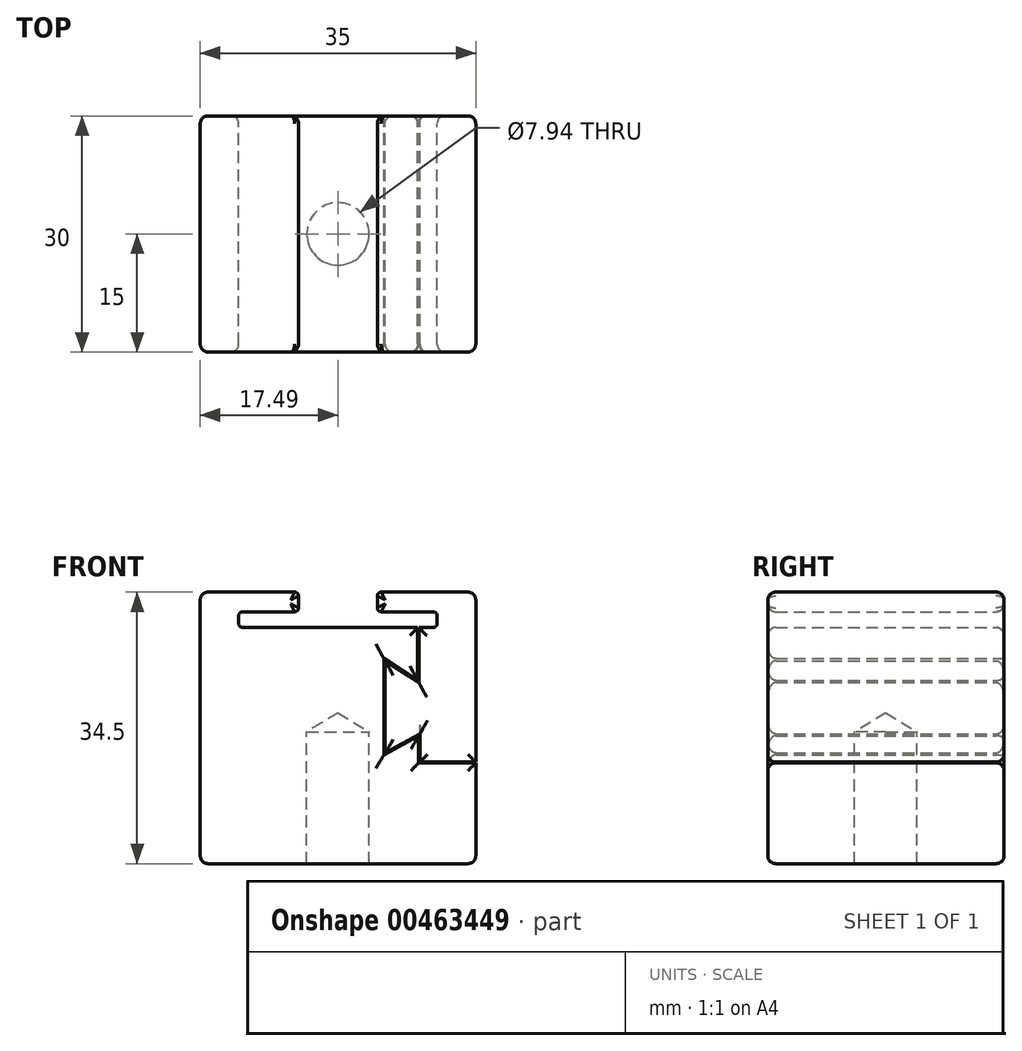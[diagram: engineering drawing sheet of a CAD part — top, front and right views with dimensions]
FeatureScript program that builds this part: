
annotation { "Feature Type Name" : "Feature", "Feature Type Description" : "" }
export const myFeature = defineFeature(function(context is Context, id is Id, definition is map)
    precondition{}
    {
        {
            var Q0;
            Q0=qCreatedBy(makeId("Front.planeOp"),FACE);
            var sketch = newSketch(context, id + "F0", { "sketchPlane" : qUnion([Q0])});
            skLineSegment(sketch, "E0.bottom", {"start": v(16.5, -15.75) * mm, "end": v(-16.5, -15.75) * mm});
            skLineSegment(sketch, "E0.top", {"start": v(16.5, 18.75) * mm, "end": v(5.5, 18.75) * mm});
            skLineSegment(sketch, "E0.left", {"start": v(17.5, -14.75) * mm, "end": v(17.5, -2.95) * mm});
            skLineSegment(sketch, "E0.right", {"start": v(-17.5, -14.75) * mm, "end": v(-17.5, 17.75) * mm});
            skPoint(sketch, "E1.middle", {"position": v(0, 0) * mm});
            skLineSegment(sketch, "E2.left", {"start": v(-5, 16.75) * mm, "end": v(-5, 18.25) * mm});
            skLineSegment(sketch, "E2.right", {"start": v(5, 16.75) * mm, "end": v(5, 18.25) * mm});
            skPoint(sketch, "E2.middle.positionSnap0", {"position": v(0, 18.75) * mm});
            skPoint(sketch, "E2.centerSnap0", {"position": v(0, 18.75) * mm});
            skLineSegment(sketch, "E3.bottom", {"start": v(12.1, 14.25) * mm, "end": v(10.29, 14.25) * mm});
            skLineSegment(sketch, "E3.top", {"start": v(12.1, 16.25) * mm, "end": v(5.5, 16.25) * mm});
            skLineSegment(sketch, "E3.left", {"start": v(12.6, 14.75) * mm, "end": v(12.6, 15.75) * mm});
            skLineSegment(sketch, "E3.right", {"start": v(-12.6, 14.75) * mm, "end": v(-12.6, 15.75) * mm});
            skPoint(sketch, "E3.middle", {"position": v(0, 15.25) * mm});
            skPoint(sketch, "E4.visualSharp", {"position": v(-12.6, 16.25) * mm});
            skArc(sketch, "E4.filletArc", {"start": v(-12.1, 16.25) * mm, "mid": v(-12.46, 16.1) * mm, "end": v(-12.6, 15.75) * mm});
            skPoint(sketch, "E5.visualSharp", {"position": v(12.6, 16.25) * mm});
            skArc(sketch, "E5.filletArc", {"start": v(12.6, 15.75) * mm, "mid": v(12.46, 16.1) * mm, "end": v(12.1, 16.25) * mm});
            skLineSegment(sketch, "E6.trimOffspring", {"start": v(-5.5, 18.75) * mm, "end": v(-16.5, 18.75) * mm});
            skLineSegment(sketch, "E7.trimOffspring", {"start": v(-5.5, 16.25) * mm, "end": v(-12.1, 16.25) * mm});
            skPoint(sketch, "E8.visualSharp", {"position": v(-12.6, 14.25) * mm});
            skArc(sketch, "E8.filletArc", {"start": v(-12.6, 14.75) * mm, "mid": v(-12.46, 14.4) * mm, "end": v(-12.1, 14.25) * mm});
            skPoint(sketch, "E9.visualSharp", {"position": v(-5, 16.25) * mm});
            skArc(sketch, "E9.filletArc", {"start": v(-5.5, 16.25) * mm, "mid": v(-5.15, 16.4) * mm, "end": v(-5, 16.75) * mm});
            skPoint(sketch, "E10.visualSharp", {"position": v(-5, 18.75) * mm});
            skArc(sketch, "E10.filletArc", {"start": v(-5, 18.25) * mm, "mid": v(-5.15, 18.6) * mm, "end": v(-5.5, 18.75) * mm});
            skPoint(sketch, "E11.visualSharp", {"position": v(5, 18.75) * mm});
            skArc(sketch, "E11.filletArc", {"start": v(5.5, 18.75) * mm, "mid": v(5.15, 18.6) * mm, "end": v(5, 18.25) * mm});
            skPoint(sketch, "E12.visualSharp", {"position": v(5, 16.25) * mm});
            skArc(sketch, "E12.filletArc", {"start": v(5, 16.75) * mm, "mid": v(5.15, 16.4) * mm, "end": v(5.5, 16.25) * mm});
            skPoint(sketch, "E13.visualSharp", {"position": v(-17.5, 18.75) * mm});
            skArc(sketch, "E13.filletArc", {"start": v(-16.5, 18.75) * mm, "mid": v(-17.2, 18.46) * mm, "end": v(-17.5, 17.75) * mm});
            skPoint(sketch, "E14.visualSharp", {"position": v(17.5, 18.75) * mm});
            skArc(sketch, "E14.filletArc", {"start": v(17.5, 17.75) * mm, "mid": v(17.22, 18.46) * mm, "end": v(16.5, 18.75) * mm});
            skPoint(sketch, "E15.visualSharp", {"position": v(12.6, 14.25) * mm});
            skArc(sketch, "E15.filletArc", {"start": v(12.1, 14.25) * mm, "mid": v(12.46, 14.4) * mm, "end": v(12.6, 14.75) * mm});
            skPoint(sketch, "E16.visualSharp", {"position": v(-17.5, -15.75) * mm});
            skArc(sketch, "E16.filletArc", {"start": v(-17.5, -14.75) * mm, "mid": v(-17.2, -15.46) * mm, "end": v(-16.5, -15.75) * mm});
            skPoint(sketch, "E17.visualSharp", {"position": v(17.5, -15.75) * mm});
            skArc(sketch, "E17.filletArc", {"start": v(16.5, -15.75) * mm, "mid": v(17.22, -15.46) * mm, "end": v(17.5, -14.75) * mm});
            skLineSegment(sketch, "E18.0", {"start": v(5.99, -1.68) * mm, "end": v(5.99, 10.03) * mm});
            skLineSegment(sketch, "E18.1", {"start": v(5.99, 10.03) * mm, "end": v(10.29, 7.25) * mm});
            skLineSegment(sketch, "E18.2", {"start": v(10.4, 0.75) * mm, "end": v(5.99, -1.68) * mm});
            skPoint(sketch, "E18.0.midPoint", {"position": v(5.99, 4.17) * mm});
            skLineSegment(sketch, "E19", {"start": v(10.29, 14.25) * mm, "end": v(10.29, 7.25) * mm});
            skLineSegment(sketch, "E20", {"start": v(10.4, 0.75) * mm, "end": v(10.4, -2.85) * mm});
            skLineSegment(sketch, "E21", {"start": v(10.4, -2.85) * mm, "end": v(17.5, -2.85) * mm});
            skLineSegment(sketch, "E22.0", {"start": v(10.25, 0.5) * mm, "end": v(10.25, -2.75) * mm});
            skLineSegment(sketch, "E22.1", {"start": v(10.14, 14.25) * mm, "end": v(10.14, 7.53) * mm});
            skLineSegment(sketch, "E22.2", {"start": v(5.84, 10.3) * mm, "end": v(10.14, 7.53) * mm});
            skLineSegment(sketch, "E22.3", {"start": v(5.84, -1.93) * mm, "end": v(5.84, 10.3) * mm});
            skLineSegment(sketch, "E22.4", {"start": v(10.25, 0.5) * mm, "end": v(5.84, -1.93) * mm});
            skLineSegment(sketch, "E23.0", {"start": v(10.45, -2.95) * mm, "end": v(17.5, -2.95) * mm});
            skLineSegment(sketch, "E24", {"start": v(10.45, -2.95) * mm, "end": v(10.25, -2.95) * mm});
            skLineSegment(sketch, "E25", {"start": v(10.25, -2.95) * mm, "end": v(10.25, -2.75) * mm});
            skLineSegment(sketch, "E26.trimOffspring", {"start": v(17.5, -2.85) * mm, "end": v(17.5, 17.75) * mm});
            skLineSegment(sketch, "E27.trimOffspring", {"start": v(10.14, 14.25) * mm, "end": v(-12.1, 14.25) * mm});
            skSolve(sketch);
        }
        {
            var Q0;
            Q0=makeQuery(id+"F0.imprint","IMPRINT",FACE,{"disambiguationData":[TD([[makeQuery(id+"F0.imprint","IMPRINT",EDGE,{"derivedFrom":sQuery(id+"F0.wireOp",EDGE,"E0.bottom")}),-1.0]])]});
            extrude(context, id + "F1", {"entities" : qUnion([Q0]), "depth" : 30 * mm, "symmetric" : true});
        }
        {
            var Q0;
            Q0=makeQuery(id+"F1.opExtrude","CAP_EDGE",EDGE,{"disambiguationData":[OSD([sQuery(id+"F0.wireOp",EDGE,"E13.filletArc")])],"isStart":true});
            var Q1;
            Q1=makeQuery(id+"F1.opExtrude","CAP_EDGE",EDGE,{"disambiguationData":[OSD([sQuery(id+"F0.wireOp",EDGE,"E13.filletArc")])],"isStart":false});
            var Q2;
            Q2=makeQuery(id+"F1.opExtrude","CAP_EDGE",EDGE,{"disambiguationData":[OSD([sQuery(id+"F0.wireOp",EDGE,"E23.0"),sQuery(id+"F0.wireOp",EDGE,"E24")])],"isStart":true});
            var Q3;
            Q3=makeQuery(id+"F1.opExtrude","CAP_EDGE",EDGE,{"disambiguationData":[OSD([sQuery(id+"F0.wireOp",EDGE,"E22.0"),sQuery(id+"F0.wireOp",EDGE,"E25")])],"isStart":true});
            var Q4;
            Q4=makeQuery(id+"F1.opExtrude","CAP_EDGE",EDGE,{"disambiguationData":[OSD([sQuery(id+"F0.wireOp",EDGE,"E22.1")])],"isStart":true});
            var Q5;
            Q5=makeQuery(id+"F1.opExtrude","CAP_EDGE",EDGE,{"disambiguationData":[OSD([sQuery(id+"F0.wireOp",EDGE,"E22.1")])],"isStart":false});
            var Q6;
            Q6=makeQuery(id+"F1.opExtrude","CAP_EDGE",EDGE,{"disambiguationData":[OSD([sQuery(id+"F0.wireOp",EDGE,"E22.0"),sQuery(id+"F0.wireOp",EDGE,"E25")])],"isStart":false});
            var Q7;
            Q7=makeQuery(id+"F1.opExtrude","CAP_EDGE",EDGE,{"disambiguationData":[OSD([sQuery(id+"F0.wireOp",EDGE,"E23.0"),sQuery(id+"F0.wireOp",EDGE,"E24")])],"isStart":false});
            var Q8;
            Q8=makeQuery(id+"F1.opExtrude","CAP_FACE",FACE,{"disambiguationData":[OSD([sQuery(id+"F0.wireOp",EDGE,"E0.bottom"),sQuery(id+"F0.wireOp",EDGE,"E0.left"),sQuery(id+"F0.wireOp",EDGE,"E0.right"),sQuery(id+"F0.wireOp",EDGE,"E2.left"),sQuery(id+"F0.wireOp",EDGE,"E3.right"),sQuery(id+"F0.wireOp",EDGE,"E4.filletArc"),sQuery(id+"F0.wireOp",EDGE,"E6.trimOffspring"),sQuery(id+"F0.wireOp",EDGE,"E7.trimOffspring"),sQuery(id+"F0.wireOp",EDGE,"E8.filletArc"),sQuery(id+"F0.wireOp",EDGE,"E9.filletArc"),sQuery(id+"F0.wireOp",EDGE,"E10.filletArc"),sQuery(id+"F0.wireOp",EDGE,"E13.filletArc"),sQuery(id+"F0.wireOp",EDGE,"E16.filletArc"),sQuery(id+"F0.wireOp",EDGE,"E17.filletArc"),sQuery(id+"F0.wireOp",EDGE,"E22.0"),sQuery(id+"F0.wireOp",EDGE,"E22.1"),sQuery(id+"F0.wireOp",EDGE,"E22.2"),sQuery(id+"F0.wireOp",EDGE,"E22.3"),sQuery(id+"F0.wireOp",EDGE,"E22.4"),sQuery(id+"F0.wireOp",EDGE,"E23.0"),sQuery(id+"F0.wireOp",EDGE,"E24"),sQuery(id+"F0.wireOp",EDGE,"E25"),sQuery(id+"F0.wireOp",EDGE,"E27.trimOffspring")])],"isStart":false});
            fillet(context, id + "F2", {"entities" : qUnion([Q0, Q1, Q2, Q3, Q4, Q5, Q6, Q7, Q8]), "radius" : 1 * mm, "tangentPropagation" : true, "allowEdgeOverflow" : false});
        }
        {
            var Q0;
            Q0=makeQuery(id+"F1.opExtrude","SWEPT_FACE",FACE,{"disambiguationData":[OSD([sQuery(id+"F0.wireOp",EDGE,"E0.bottom")])]});
            var sketch = newSketch(context, id + "F3", { "sketchPlane" : qUnion([Q0])});
            skPoint(sketch, "E28", {"position": v(0, 0) * mm});
            skSolve(sketch);
        }
        {
            var Q0;
            Q0=sQuery(id+"F3.wireOp",VERTEX,"E28");
            var Q1;
            Q1=makeQuery(id+"F1.opExtrude","SWEPT_BODY",BODY,{"disambiguationData":[OSD([sQuery(id+"F0.wireOp",EDGE,"E0.bottom"),sQuery(id+"F0.wireOp",EDGE,"E0.top"),sQuery(id+"F0.wireOp",EDGE,"E0.left"),sQuery(id+"F0.wireOp",EDGE,"E0.right"),sQuery(id+"F0.wireOp",EDGE,"E2.left"),sQuery(id+"F0.wireOp",EDGE,"E2.right"),sQuery(id+"F0.wireOp",EDGE,"E3.bottom"),sQuery(id+"F0.wireOp",EDGE,"E3.top"),sQuery(id+"F0.wireOp",EDGE,"E3.left"),sQuery(id+"F0.wireOp",EDGE,"E3.right"),sQuery(id+"F0.wireOp",EDGE,"E4.filletArc"),sQuery(id+"F0.wireOp",EDGE,"E5.filletArc"),sQuery(id+"F0.wireOp",EDGE,"E6.trimOffspring"),sQuery(id+"F0.wireOp",EDGE,"E7.trimOffspring"),sQuery(id+"F0.wireOp",EDGE,"E8.filletArc"),sQuery(id+"F0.wireOp",EDGE,"E9.filletArc"),sQuery(id+"F0.wireOp",EDGE,"E10.filletArc"),sQuery(id+"F0.wireOp",EDGE,"E11.filletArc"),sQuery(id+"F0.wireOp",EDGE,"E12.filletArc"),sQuery(id+"F0.wireOp",EDGE,"E13.filletArc"),sQuery(id+"F0.wireOp",EDGE,"E14.filletArc"),sQuery(id+"F0.wireOp",EDGE,"E15.filletArc"),sQuery(id+"F0.wireOp",EDGE,"E16.filletArc"),sQuery(id+"F0.wireOp",EDGE,"E17.filletArc")])]});
            hole(context, id + "F4", {"style" : HoleStyle.SIMPLE, "endStyle" : HoleEndStyle.BLIND, "standardTappedOrClearance" : lookupTablePath({ "standard" : "ANSI", "engagement" : "75%", "pitch" : "16 tpi", "size" : "3/8", "type" : "Tapped" }), "standardBlindInLast" : lookupTablePath({ "standard" : "ANSI", "engagement" : "75%", "pitch" : "16 tpi", "size" : "3/8", "type" : "Tapped" }), "holeDiameter" : 7.94 * mm, "showTappedDepth" : true, "holeDepth" : 16.76 * mm, "isTappedThrough" : true, "tappedDepth" : 12 * mm, "tapClearance" : 3, "startFromSketch" : true, "locations" : qUnion([Q0]), "scope" : qUnion([Q1]), "majorDiameter" : 9.53 * mm});
        }
        {
            var Q0;
            Q0=makeQuery(id+"F0.imprint","IMPRINT",FACE,{"disambiguationData":[TD([[makeQuery(id+"F0.imprint","IMPRINT",EDGE,{"derivedFrom":sQuery(id+"F0.wireOp",EDGE,"E0.top")}),1.0]])]});
            extrude(context, id + "F5", {"entities" : qUnion([Q0]), "depth" : 30 * mm, "symmetric" : true});
        }
        {
            var Q0;
            Q0=makeQuery(id+"F5.opExtrude","CAP_EDGE",EDGE,{"disambiguationData":[OSD([sQuery(id+"F0.wireOp",EDGE,"E0.top")])],"isStart":false});
            var Q1;
            Q1=makeQuery(id+"F5.opExtrude","CAP_EDGE",EDGE,{"disambiguationData":[OSD([sQuery(id+"F0.wireOp",EDGE,"E18.0")])],"isStart":false});
            var Q2;
            Q2=makeQuery(id+"F5.opExtrude","CAP_EDGE",EDGE,{"disambiguationData":[OSD([sQuery(id+"F0.wireOp",EDGE,"E0.top")])],"isStart":true});
            var Q3;
            Q3=makeQuery(id+"F5.opExtrude","CAP_EDGE",EDGE,{"disambiguationData":[OSD([sQuery(id+"F0.wireOp",EDGE,"E21")])],"isStart":true});
            var Q4;
            Q4=makeQuery(id+"F5.opExtrude","CAP_EDGE",EDGE,{"disambiguationData":[OSD([sQuery(id+"F0.wireOp",EDGE,"E18.2")])],"isStart":true});
            var Q5;
            Q5=makeQuery(id+"F5.opExtrude","CAP_EDGE",EDGE,{"disambiguationData":[OSD([sQuery(id+"F0.wireOp",EDGE,"E18.0")])],"isStart":true});
            var Q6;
            Q6=makeQuery(id+"F5.opExtrude","CAP_EDGE",EDGE,{"disambiguationData":[OSD([sQuery(id+"F0.wireOp",EDGE,"E18.1")])],"isStart":true});
            var Q7;
            Q7=makeQuery(id+"F5.opExtrude","CAP_EDGE",EDGE,{"disambiguationData":[OSD([sQuery(id+"F0.wireOp",EDGE,"E19")])],"isStart":true});
            var Q8;
            Q8=makeQuery(id+"F5.opExtrude","CAP_EDGE",EDGE,{"disambiguationData":[OSD([sQuery(id+"F0.wireOp",EDGE,"E19")])],"isStart":false});
            var Q9;
            Q9=makeQuery(id+"F5.opExtrude","CAP_EDGE",EDGE,{"disambiguationData":[OSD([sQuery(id+"F0.wireOp",EDGE,"E18.1")])],"isStart":false});
            var Q10;
            Q10=makeQuery(id+"F5.opExtrude","CAP_EDGE",EDGE,{"disambiguationData":[OSD([sQuery(id+"F0.wireOp",EDGE,"E18.2")])],"isStart":false});
            var Q11;
            Q11=makeQuery(id+"F5.opExtrude","CAP_EDGE",EDGE,{"disambiguationData":[OSD([sQuery(id+"F0.wireOp",EDGE,"E20")])],"isStart":false});
            var Q12;
            Q12=makeQuery(id+"F5.opExtrude","CAP_EDGE",EDGE,{"disambiguationData":[OSD([sQuery(id+"F0.wireOp",EDGE,"E21")])],"isStart":false});
            fillet(context, id + "F6", {"entities" : qUnion([Q0, Q1, Q2, Q3, Q4, Q5, Q6, Q7, Q8, Q9, Q10, Q11, Q12]), "radius" : 1 * mm, "tangentPropagation" : true, "allowEdgeOverflow" : false});
        }
    });
